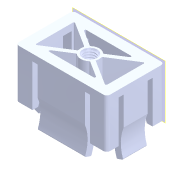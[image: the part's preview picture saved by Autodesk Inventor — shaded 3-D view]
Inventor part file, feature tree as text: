
AUTODESK INVENTOR PART (.ipt)
format: ipt  version: 2021 (Build 250183000, 183)  size: 426,496 bytes
history: native  units: mm
features: plane x1, split x1, other x1
ambient origin geometry x8: Origin, YZ Plane, XZ Plane, XY Plane, X Axis, Y Axis, Z Axis, Center Point
bodies: Solid1 (feature_tree)
feature tree (3):
  plane  "Work Plane1"
  split  "Split1"
  other  "Austragung1"
